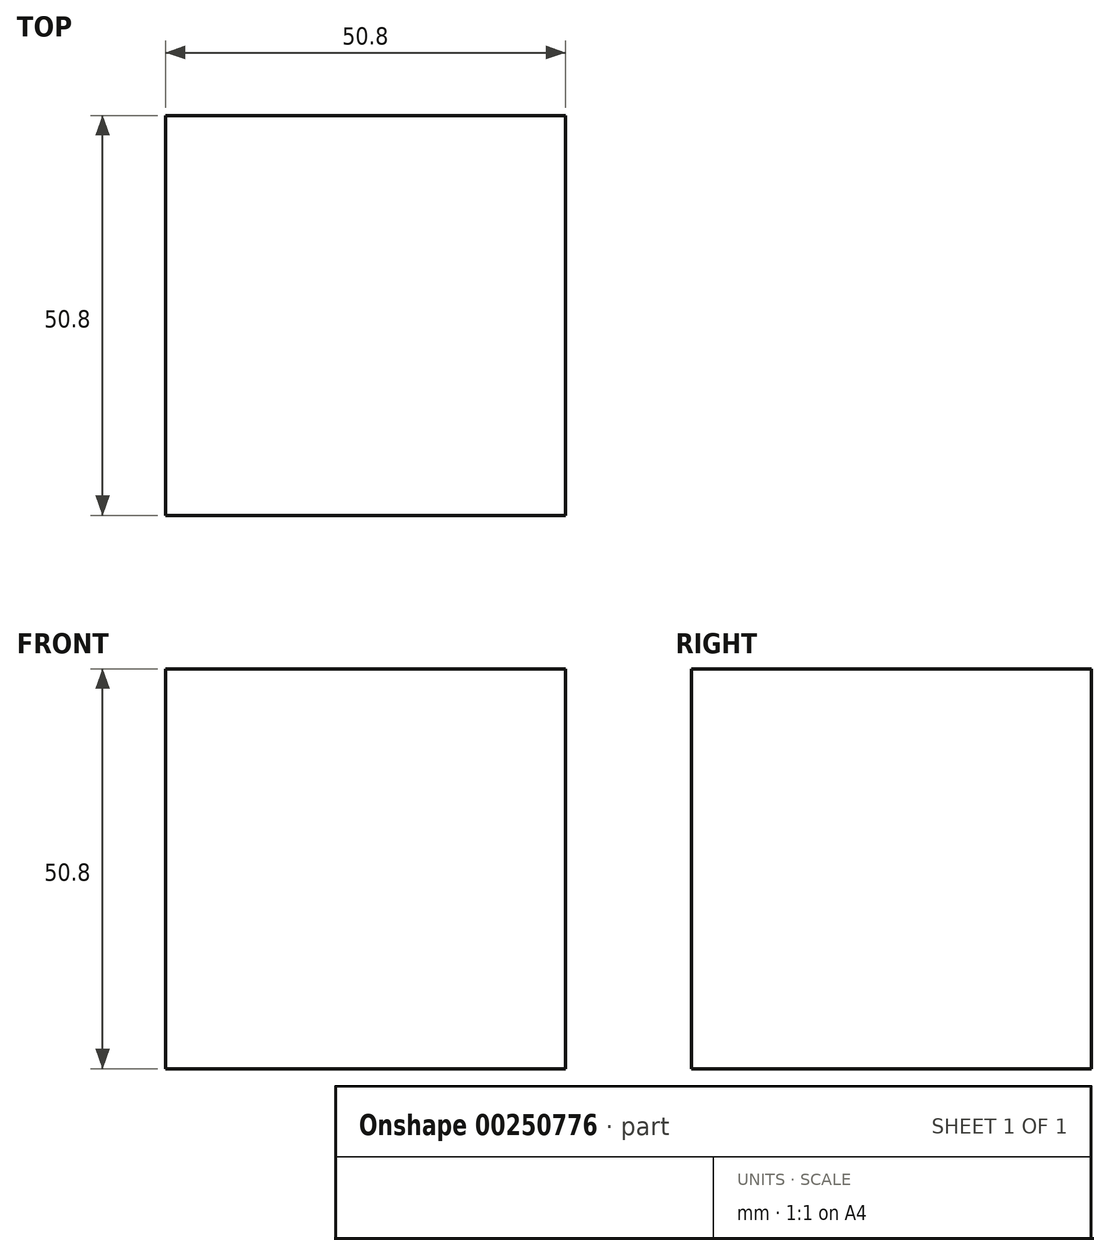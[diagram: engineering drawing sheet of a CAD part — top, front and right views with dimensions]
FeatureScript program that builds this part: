
annotation { "Feature Type Name" : "Feature", "Feature Type Description" : "" }
export const myFeature = defineFeature(function(context is Context, id is Id, definition is map)
    precondition{}
    {
        {
            var Q0;
            Q0=qCreatedBy(makeId("Front.planeOp"),FACE);
            var sketch = newSketch(context, id + "F0", { "sketchPlane" : qUnion([Q0])});
            skLineSegment(sketch, "E0.bottom", {"start": v(-25.4, -25.4) * mm, "end": v(25.4, -25.4) * mm});
            skLineSegment(sketch, "E0.top", {"start": v(-25.4, 25.4) * mm, "end": v(25.4, 25.4) * mm});
            skLineSegment(sketch, "E0.left", {"start": v(-25.4, -25.4) * mm, "end": v(-25.4, 25.4) * mm});
            skLineSegment(sketch, "E0.right", {"start": v(25.4, -25.4) * mm, "end": v(25.4, 25.4) * mm});
            skPoint(sketch, "E0.middle", {"position": v(0, 0) * mm});
            skSolve(sketch);
        }
        {
            var Q0;
            Q0 = qSketchRegion(id + "F0", true);
            extrude(context, id + "F1", {"entities" : qUnion([Q0]), "endBound" : BoundingType.SYMMETRIC, "depth" : 50.8 * mm});
        }
    });
